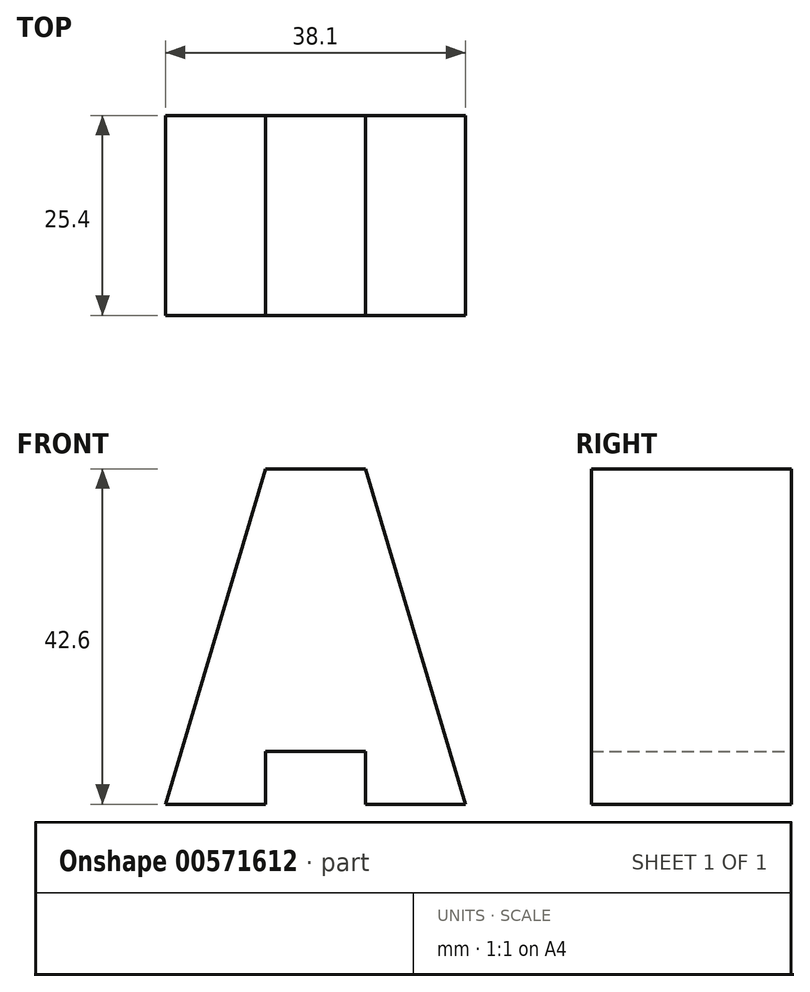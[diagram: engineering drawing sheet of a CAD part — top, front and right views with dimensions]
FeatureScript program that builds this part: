
annotation { "Feature Type Name" : "Feature", "Feature Type Description" : "" }
export const myFeature = defineFeature(function(context is Context, id is Id, definition is map)
    precondition{}
    {
        {
            var Q0;
            Q0=qCreatedBy(makeId("Front.planeOp"),FACE);
            var sketch = newSketch(context, id + "F0", { "sketchPlane" : qUnion([Q0])});
            skLineSegment(sketch, "E0", {"start": v(-39.17, 73) * mm, "end": v(-26.47, 73) * mm});
            skLineSegment(sketch, "E1", {"start": v(-39.17, 73) * mm, "end": v(-51.87, 30.4) * mm});
            skLineSegment(sketch, "E2", {"start": v(-51.87, 30.4) * mm, "end": v(-13.77, 30.4) * mm});
            skLineSegment(sketch, "E3", {"start": v(-26.47, 73) * mm, "end": v(-13.77, 30.4) * mm});
            skLineSegment(sketch, "E4", {"start": v(-39.17, 30.4) * mm, "end": v(-39.17, 37.1) * mm});
            skLineSegment(sketch, "E5", {"start": v(-39.17, 37.1) * mm, "end": v(-26.47, 37.1) * mm});
            skLineSegment(sketch, "E6", {"start": v(-26.47, 37.1) * mm, "end": v(-26.47, 30.4) * mm});
            skSolve(sketch);
        }
        {
            var Q0;
            Q0=makeQuery(id+"F0.imprint","IMPRINT",FACE,{"disambiguationData":[TD([[makeQuery(id+"F0.imprint","IMPRINT",EDGE,{"derivedFrom":sQuery(id+"F0.wireOp",EDGE,"E0")}),-1.0]])]});
            extrude(context, id + "F1", {"entities" : qUnion([Q0]), "depth" : 25.4 * mm, "offsetDistance" : 25.4 * mm});
        }
    });
